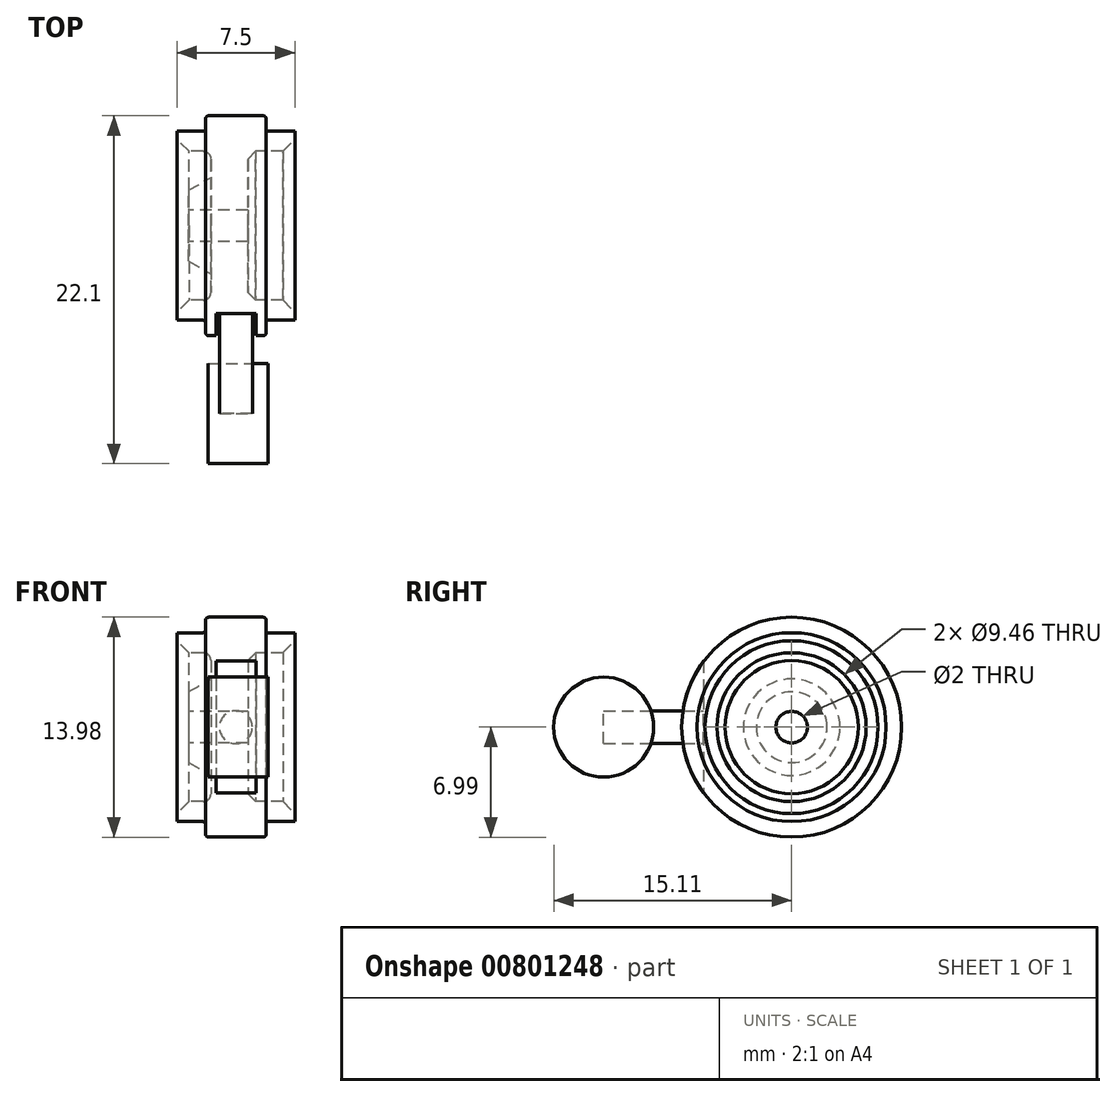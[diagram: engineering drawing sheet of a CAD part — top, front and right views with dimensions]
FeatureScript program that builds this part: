
annotation { "Feature Type Name" : "Feature", "Feature Type Description" : "" }
export const myFeature = defineFeature(function(context is Context, id is Id, definition is map)
    precondition{}
    {
        {
            var Q0;
            Q0=qCreatedBy(makeId("Front.planeOp"),FACE);
            var sketch = newSketch(context, id + "F0", { "sketchPlane" : qUnion([Q0])});
            skLineSegment(sketch, "E0", {"start": v(-3, 1) * mm, "end": v(0.76, 1) * mm});
            skLineSegment(sketch, "E1", {"start": v(0.76, 1) * mm, "end": v(0.76, 4.23) * mm});
            skLineSegment(sketch, "E2", {"start": v(1.26, 4.73) * mm, "end": v(3.75, 4.73) * mm});
            skLineSegment(sketch, "E3", {"start": v(3.75, 4.73) * mm, "end": v(3.75, 6) * mm});
            skLineSegment(sketch, "E4", {"start": v(3.75, 6) * mm, "end": v(1.92, 6) * mm});
            skLineSegment(sketch, "E5", {"start": v(-1.92, 6.99) * mm, "end": v(-1.92, 6) * mm});
            skLineSegment(sketch, "E6", {"start": v(-1.92, 6) * mm, "end": v(-3.75, 6) * mm});
            skLineSegment(sketch, "E7", {"start": v(-3.75, 6) * mm, "end": v(-3.75, 4.73) * mm});
            skLineSegment(sketch, "E8", {"start": v(-1.59, 3.07) * mm, "end": v(-3, 2.25) * mm});
            skLineSegment(sketch, "E9", {"start": v(-3, 2.25) * mm, "end": v(-3, 1) * mm});
            skLineSegment(sketch, "E10", {"start": v(0, 6.99) * mm, "end": v(0, 0) * mm, "construction": true});
            skLineSegment(sketch, "E11", {"start": v(0, 0) * mm, "end": v(34.63, 0) * mm});
            skLineSegment(sketch, "E12.left", {"start": v(1.92, 6.99) * mm, "end": v(1.92, 6) * mm});
            skLineSegment(sketch, "E13.trimOffspring", {"start": v(1.92, 6.99) * mm, "end": v(-1.92, 6.99) * mm});
            skLineSegment(sketch, "E14", {"start": v(-1.59, 3.07) * mm, "end": v(-1.59, 4.23) * mm});
            skArc(sketch, "E15.filletArc", {"start": v(-1.59, 4.23) * mm, "mid": v(-1.73, 4.58) * mm, "end": v(-2.09, 4.73) * mm});
            skLineSegment(sketch, "E16", {"start": v(0.76, 4.23) * mm, "end": v(1.26, 4.73) * mm});
            skLineSegment(sketch, "E17", {"start": v(-3.75, 5.37) * mm, "end": v(0, 5.37) * mm, "construction": true});
            skLineSegment(sketch, "E18", {"start": v(0, 5.37) * mm, "end": v(3.75, 5.37) * mm, "construction": true});
            skLineSegment(sketch, "E19", {"start": v(-3.75, 4.73) * mm, "end": v(-2.09, 4.73) * mm});
            skSolve(sketch);
        }
        {
            var Q0;
            Q0=qSketchRegion(id+"F0",true);
            var Q1;
            Q1=sQuery(id+"F0.wireOp",EDGE,"E11");
            revolve(context, id + "F1", {"surfaceOperationType" : NewSurfaceOperationType.NEW, "entities" : qUnion([Q0]), "axis" : qUnion([Q1]), "revolveType" : RevolveType.FULL});
        }
        {
            var Q0;
            Q0=makeQuery(id+"F1.opRevolve","SWEPT_EDGE",EDGE,{"disambiguationData":[OSD([sQuery(id+"F0.wireOp",EDGE,"aKgQp8U8-3RdW-JoUc-8vtd-pMIEm6OBKysV"),sQuery(id+"F0.wireOp",EDGE,"Nlnvn1ff-qTJJ-98mA-zu21-zmskdIcCKw7V")])]});
            var Q1;
            Q1=makeQuery(id+"F1.opRevolve","SWEPT_EDGE",EDGE,{"disambiguationData":[OSD([sQuery(id+"F0.wireOp",EDGE,"Nlnvn1ff-qTJJ-98mA-zu21-zmskdIcCKw7V"),sQuery(id+"F0.wireOp",EDGE,"E5")])]});
            var Q2;
            Q2=makeQuery(id+"F1.opRevolve","SWEPT_EDGE",EDGE,{"disambiguationData":[OSD([sQuery(id+"F0.wireOp",EDGE,"E12.left"),sQuery(id+"F0.wireOp",EDGE,"E13.trimOffspring")])]});
            fillet(context, id + "F2", {"entities" : qUnion([Q0, Q1, Q2]), "radius" : 0.2 * mm, "tangentPropagation" : true, "allowEdgeOverflow" : false});
        }
        {
            var Q0;
            Q0=makeQuery(id+"F1.opRevolve","SWEPT_EDGE",EDGE,{"disambiguationData":[OSD([sQuery(id+"F0.wireOp",EDGE,"E2"),sQuery(id+"F0.wireOp",EDGE,"E3")])]});
            var Q1;
            Q1=makeQuery(id+"F1.opRevolve","SWEPT_EDGE",EDGE,{"disambiguationData":[OSD([sQuery(id+"F0.wireOp",EDGE,"E7"),sQuery(id+"F0.wireOp",EDGE,"E19")])]});
            chamfer(context, id + "F3", {"entities" : qUnion([Q0, Q1]), "width" : 0.76 * mm, "tangentPropagation" : true});
        }
        {
            var Q0;
            Q0=qCreatedBy(makeId("Right.planeOp"),FACE);
            var sketch = newSketch(context, id + "F4", { "sketchPlane" : qUnion([Q0])});
            skLineSegment(sketch, "E20.bottom", {"start": v(-10.48, 5.78) * mm, "end": v(-5.59, 5.78) * mm});
            skLineSegment(sketch, "E20.top", {"start": v(-10.48, -5.81) * mm, "end": v(-5.59, -5.81) * mm});
            skLineSegment(sketch, "E20.left", {"start": v(-10.48, 5.78) * mm, "end": v(-10.48, -5.81) * mm});
            skLineSegment(sketch, "E20.right", {"start": v(-5.59, 5.78) * mm, "end": v(-5.59, -5.81) * mm});
            skSolve(sketch);
        }
        {
            var Q0;
            Q0=qSketchRegion(id+"F4",true);
            extrude(context, id + "F5", {"entities" : qUnion([Q0]), "operationType" : NewBodyOperationType.REMOVE, "oppositeDirection" : true, "depth" : 2.54 * mm, "offsetDistance" : 25.4 * mm, "symmetric" : true});
        }
        {
            var Q0;
            Q0=makeQuery(id+"F5.boolean.opBoolean","COPY",FACE,{"derivedFrom":makeQuery(id+"F5.opExtrude","SWEPT_FACE",FACE,{"disambiguationData":[OSD([sQuery(id+"F4.wireOp",EDGE,"E20.right")])]})});
            var sketch = newSketch(context, id + "F6", { "sketchPlane" : qUnion([Q0])});
            skCircle(sketch, "E21", {"center": v(0, 0) * mm, "radius": 1.05 * mm});
            skSolve(sketch);
        }
        {
            var Q0;
            Q0=qSketchRegion(id+"F6",true);
            extrude(context, id + "F7", {"entities" : qUnion([Q0]), "operationType" : NewBodyOperationType.ADD, "depth" : 6.35 * mm, "offsetDistance" : 25.4 * mm});
        }
        {
            var Q0;
            Q0=makeQuery(id+"F7.opExtrude","CAP_FACE",FACE,{"disambiguationData":[OSD([sQuery(id+"F6.wireOp",EDGE,"E21")])],"isStart":false});
            var sketch = newSketch(context, id + "F8", { "sketchPlane" : qUnion([Q0])});
            skLineSegment(sketch, "E22", {"start": v(-1.05, 0) * mm, "end": v(1.05, 0) * mm});
            skSolve(sketch);
        }
        {
            var Q0;
            Q0=makeQuery(id+"F1.opRevolve","SWEPT_FACE",FACE,{"disambiguationData":[OSD([sQuery(id+"F0.wireOp",EDGE,"E1")])]});
            var sketch = newSketch(context, id + "F9", { "sketchPlane" : qUnion([Q0])});
            skCircle(sketch, "E23", {"center": v(-11.94, 0) * mm, "radius": 3.17 * mm});
            skLineSegment(sketch, "E24", {"start": v(-11.94, 0) * mm, "end": v(0, 0) * mm, "construction": true});
            skLineSegment(sketch, "E25", {"start": v(-11.94, 0) * mm, "end": v(-23.88, 0) * mm, "construction": true});
            skSolve(sketch);
        }
        {
            var Q0;
            Q0=qSketchRegion(id+"F9",true);
            extrude(context, id + "F10", {"entities" : qUnion([Q0]), "oppositeDirection" : true, "depth" : 2.54 * mm, "offsetDistance" : 25.4 * mm, "hasSecondDirection" : true, "secondDirectionOppositeDirection" : false, "secondDirectionDepth" : 1.27 * mm});
        }
    });
